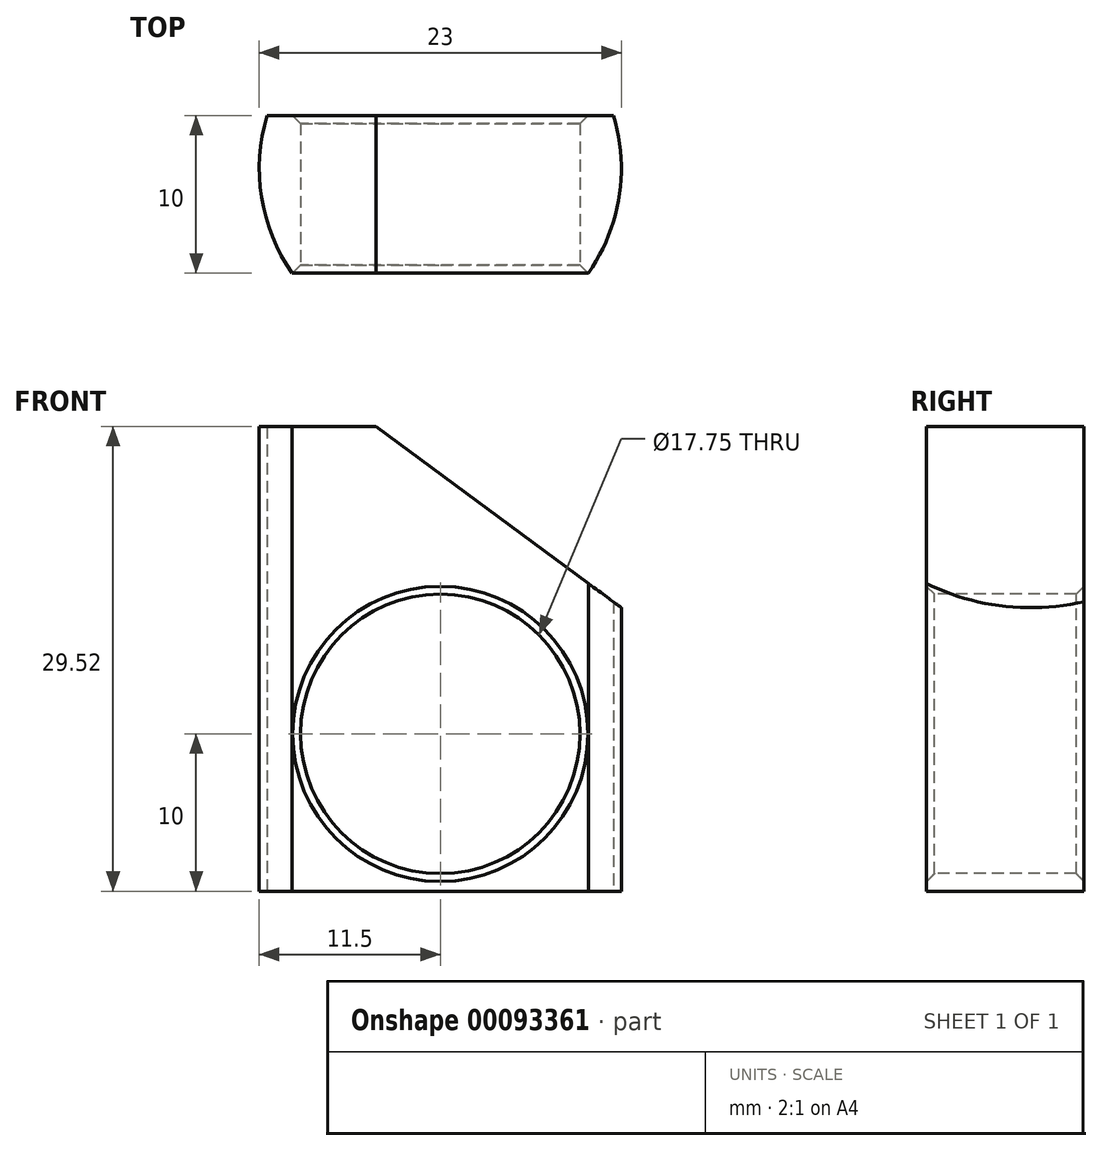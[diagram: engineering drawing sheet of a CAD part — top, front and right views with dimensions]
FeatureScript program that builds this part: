
annotation { "Feature Type Name" : "Feature", "Feature Type Description" : "" }
export const myFeature = defineFeature(function(context is Context, id is Id, definition is map)
    precondition{}
    {
        {
            var Q0;
            Q0=qCreatedBy(makeId("Front.planeOp"),FACE);
            var sketch = newSketch(context, id + "F0", { "sketchPlane" : qUnion([Q0])});
            skCircle(sketch, "E0", {"center": v(0, 0) * mm, "radius": 8.88 * mm});
            skSolve(sketch);
        }
        {
            var Q0;
            Q0=qCreatedBy(makeId("Top.planeOp"),FACE);
            var sketch = newSketch(context, id + "F1", { "sketchPlane" : qUnion([Q0])});
            skCircle(sketch, "E1", {"center": v(0, 0) * mm, "radius": 11.5 * mm});
            skSolve(sketch);
        }
        {
            var Q0;
            Q0 = qSketchRegion(id + "F1", true);
            extrude(context, id + "F2", {"entities" : qUnion([Q0]), "depth" : 19.52 * mm, "hasSecondDirection" : true, "secondDirectionOppositeDirection" : true, "secondDirectionDepth" : 10 * mm});
        }
        {
            var Q0;
            Q0 = qSketchRegion(id + "F0", true);
            extrude(context, id + "F3", {"entities" : qUnion([Q0]), "operationType" : NewBodyOperationType.REMOVE, "oppositeDirection" : true, "depth" : 25 * mm, "hasSecondDirection" : true, "secondDirectionOppositeDirection" : false, "secondDirectionDepth" : 25 * mm});
        }
        {
            var Q0;
            Q0=qCreatedBy(makeId("Front.planeOp"),FACE);
            var sketch = newSketch(context, id + "F4", { "sketchPlane" : qUnion([Q0])});
            skLineSegment(sketch, "E2", {"start": v(-16.33, 28.55) * mm, "end": v(24.77, -1.78) * mm});
            skLineSegment(sketch, "E3", {"start": v(24.77, -1.78) * mm, "end": v(24.77, 28.55) * mm});
            skLineSegment(sketch, "E4", {"start": v(24.77, 28.55) * mm, "end": v(-16.33, 28.55) * mm});
            skSolve(sketch);
        }
        {
            var Q0;
            Q0 = qSketchRegion(id + "F4", true);
            extrude(context, id + "F5", {"entities" : qUnion([Q0]), "operationType" : NewBodyOperationType.REMOVE, "oppositeDirection" : true, "depth" : 25 * mm, "hasSecondDirection" : true, "secondDirectionOppositeDirection" : false, "secondDirectionDepth" : 25 * mm});
        }
        {
            var Q0;
            Q0=qCreatedBy(makeId("Top.planeOp"),FACE);
            var sketch = newSketch(context, id + "F6", { "sketchPlane" : qUnion([Q0])});
            skLineSegment(sketch, "E5.bottom", {"start": v(-13.62, -6.62) * mm, "end": v(17.44, -6.62) * mm});
            skLineSegment(sketch, "E5.top", {"start": v(-13.62, 3.38) * mm, "end": v(17.44, 3.38) * mm});
            skLineSegment(sketch, "E5.left", {"start": v(-13.62, -6.62) * mm, "end": v(-13.62, 3.38) * mm});
            skLineSegment(sketch, "E5.right", {"start": v(17.44, -6.62) * mm, "end": v(17.44, 3.38) * mm});
            skLineSegment(sketch, "E6", {"start": v(-13.62, 3.38) * mm, "end": v(-13.62, 17.25) * mm});
            skLineSegment(sketch, "E7", {"start": v(-13.62, 17.25) * mm, "end": v(17.44, 17.25) * mm});
            skLineSegment(sketch, "E8", {"start": v(17.44, 17.25) * mm, "end": v(17.44, 3.38) * mm});
            skLineSegment(sketch, "E9", {"start": v(-13.62, -6.62) * mm, "end": v(-13.62, -19.8) * mm});
            skLineSegment(sketch, "E10", {"start": v(-13.62, -19.8) * mm, "end": v(17.44, -19.8) * mm});
            skLineSegment(sketch, "E11", {"start": v(17.44, -19.8) * mm, "end": v(17.44, -6.62) * mm});
            skSolve(sketch);
        }
        {
            var Q0;
            Q0=makeQuery(id+"F6.imprint","IMPRINT",FACE,{"disambiguationData":[TD([[makeQuery(id+"F6.imprint","IMPRINT",EDGE,{"derivedFrom":sQuery(id+"F6.wireOp",EDGE,"E5.top")}),1.0]])]});
            var Q1;
            Q1=makeQuery(id+"F6.imprint","IMPRINT",FACE,{"disambiguationData":[TD([[makeQuery(id+"F6.imprint","IMPRINT",EDGE,{"derivedFrom":sQuery(id+"F6.wireOp",EDGE,"E5.bottom")}),-1.0]])]});
            extrude(context, id + "F7", {"entities" : qUnion([Q0, Q1]), "operationType" : NewBodyOperationType.REMOVE, "oppositeDirection" : true, "depth" : 25 * mm, "hasSecondDirection" : true, "secondDirectionOppositeDirection" : false, "secondDirectionDepth" : 25 * mm});
        }
        {
            var Q0;
            Q0=makeQuery(id+"F7.boolean.opBoolean","INTERSECT",EDGE,{"derivedFrom":[makeQuery(id+"F3.boolean.opBoolean","COPY",FACE,{"derivedFrom":makeQuery(id+"F3.opExtrude","SWEPT_FACE",FACE,{"disambiguationData":[OSD([sQuery(id+"F0.wireOp",EDGE,"E0")])]})}),makeQuery(id+"F7.opExtrude","SWEPT_FACE",FACE,{"disambiguationData":[OSD([sQuery(id+"F6.wireOp",EDGE,"E5.top")])]})]});
            var Q1;
            Q1=makeQuery(id+"F7.boolean.opBoolean","INTERSECT",EDGE,{"derivedFrom":[makeQuery(id+"F3.boolean.opBoolean","COPY",FACE,{"derivedFrom":makeQuery(id+"F3.opExtrude","SWEPT_FACE",FACE,{"disambiguationData":[OSD([sQuery(id+"F0.wireOp",EDGE,"E0")])]})}),makeQuery(id+"F7.opExtrude","SWEPT_FACE",FACE,{"disambiguationData":[OSD([sQuery(id+"F6.wireOp",EDGE,"E5.bottom")])]})]});
            chamfer(context, id + "F8", {"entities" : qUnion([Q0, Q1]), "width" : .5 * mm, "tangentPropagation" : true});
        }
    });
